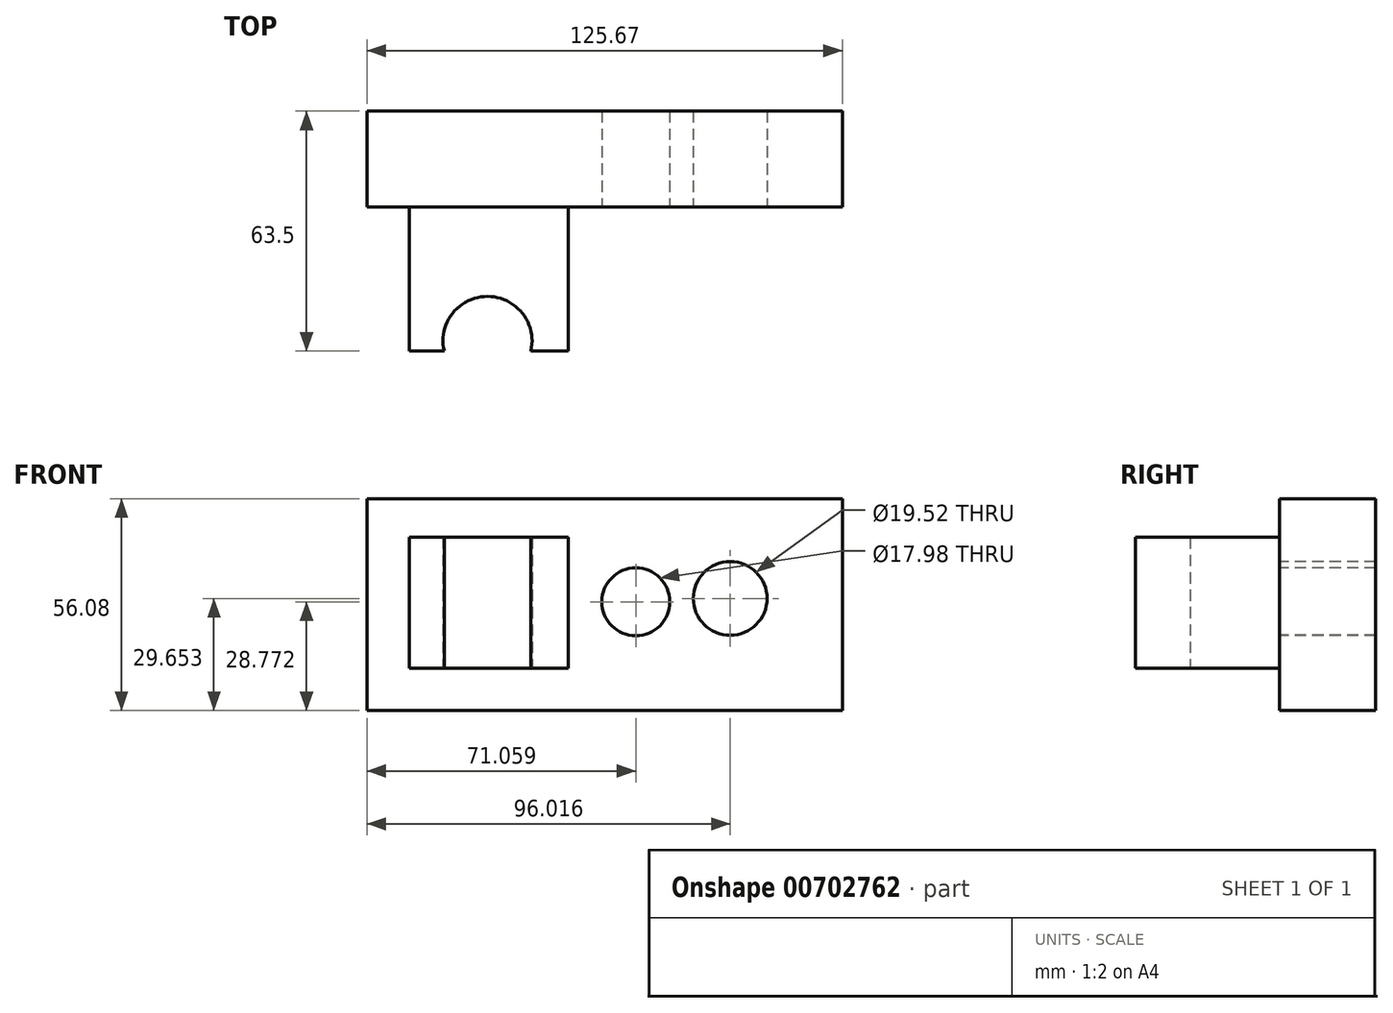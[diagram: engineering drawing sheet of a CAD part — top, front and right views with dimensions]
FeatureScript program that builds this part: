
annotation { "Feature Type Name" : "Feature", "Feature Type Description" : "" }
export const myFeature = defineFeature(function(context is Context, id is Id, definition is map)
    precondition{}
    {
        {
            var Q0;
            Q0=qCreatedBy(makeId("Front.planeOp"),FACE);
            var sketch = newSketch(context, id + "F0", { "sketchPlane" : qUnion([Q0])});
            skLineSegment(sketch, "E0.bottom", {"start": v(-61.8, 36.4) * mm, "end": v(63.86, 36.4) * mm});
            skLineSegment(sketch, "E0.top", {"start": v(-61.8, -19.67) * mm, "end": v(63.86, -19.67) * mm});
            skLineSegment(sketch, "E0.left", {"start": v(-61.8, 36.4) * mm, "end": v(-61.8, -19.67) * mm});
            skLineSegment(sketch, "E0.right", {"start": v(63.86, 36.4) * mm, "end": v(63.86, -19.67) * mm});
            skSolve(sketch);
        }
        {
            var Q0;
            Q0 = qSketchRegion(id + "F0", true);
            extrude(context, id + "F1", {"entities" : qUnion([Q0]), "depth" : 25.4 * mm, "offsetDistance" : 25.4 * mm});
        }
        {
            var Q0;
            Q0=makeQuery(id+"F1.opExtrude","CAP_FACE",FACE,{"disambiguationData":[OSD([sQuery(id+"F0.wireOp",EDGE,"E0.bottom"),sQuery(id+"F0.wireOp",EDGE,"E0.top"),sQuery(id+"F0.wireOp",EDGE,"E0.left"),sQuery(id+"F0.wireOp",EDGE,"E0.right")])],"isStart":false});
            var sketch = newSketch(context, id + "F2", { "sketchPlane" : qUnion([Q0])});
            skLineSegment(sketch, "E1.bottom", {"start": v(-50.65, 26.13) * mm, "end": v(-8.66, 26.13) * mm});
            skLineSegment(sketch, "E1.top", {"start": v(-50.65, -8.51) * mm, "end": v(-8.66, -8.51) * mm});
            skLineSegment(sketch, "E1.left", {"start": v(-50.65, 26.13) * mm, "end": v(-50.65, -8.51) * mm});
            skLineSegment(sketch, "E1.right", {"start": v(-8.66, 26.13) * mm, "end": v(-8.66, -8.51) * mm});
            skSolve(sketch);
        }
        {
            var Q0;
            Q0 = qSketchRegion(id + "F2", true);
            extrude(context, id + "F3", {"entities" : qUnion([Q0]), "operationType" : NewBodyOperationType.ADD, "depth" : 38.1 * mm, "offsetDistance" : 25.4 * mm});
        }
        {
            var Q0;
            Q0=makeQuery(id+"F3.opExtrude","SWEPT_FACE",FACE,{"disambiguationData":[OSD([sQuery(id+"F2.wireOp",EDGE,"E1.top")])]});
            var sketch = newSketch(context, id + "F4", { "sketchPlane" : qUnion([Q0])});
            skArc(sketch, "E2", {"start": v(-41.42, 63.5) * mm, "mid": v(-29.97, 49) * mm, "end": v(-18.52, 63.5) * mm});
            skLineSegment(sketch, "E3", {"start": v(-41.42, 63.5) * mm, "end": v(-18.52, 63.5) * mm});
            skSolve(sketch);
        }
        {
            var Q0;
            Q0 = qSketchRegion(id + "F4", true);
            extrude(context, id + "F5", {"entities" : qUnion([Q0]), "operationType" : NewBodyOperationType.REMOVE, "oppositeDirection" : true, "depth" : 50.8 * mm, "offsetDistance" : 25.4 * mm});
        }
        {
            var Q0;
            Q0=makeQuery(id+"F1.opExtrude","CAP_FACE",FACE,{"disambiguationData":[OSD([sQuery(id+"F0.wireOp",EDGE,"E0.bottom"),sQuery(id+"F0.wireOp",EDGE,"E0.top"),sQuery(id+"F0.wireOp",EDGE,"E0.left"),sQuery(id+"F0.wireOp",EDGE,"E0.right")])],"isStart":false});
            var sketch = newSketch(context, id + "F6", { "sketchPlane" : qUnion([Q0])});
            skCircle(sketch, "E4", {"center": v(9.25, 9.1) * mm, "radius": 8.99 * mm});
            skCircle(sketch, "E5", {"center": v(34.2, 9.98) * mm, "radius": 9.76 * mm});
            skSolve(sketch);
        }
        {
            var Q0;
            Q0 = qSketchRegion(id + "F6", true);
            extrude(context, id + "F7", {"entities" : qUnion([Q0]), "operationType" : NewBodyOperationType.REMOVE, "oppositeDirection" : true, "depth" : 50.8 * mm, "offsetDistance" : 25.4 * mm});
        }
    });
